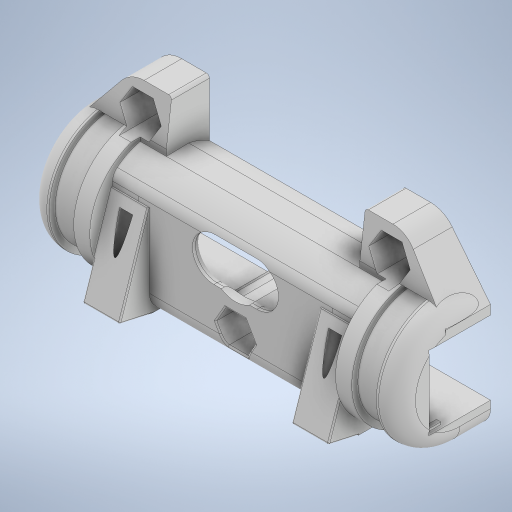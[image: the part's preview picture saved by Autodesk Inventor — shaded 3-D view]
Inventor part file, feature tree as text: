
AUTODESK INVENTOR PART (.ipt)
format: ipt  version: 2023 (Build 270158000, 158)  size: 2,027,008 bytes
history: native  units: mm
features: extrude x61, projected_geometry x60, sketch x41, fillet x6, mirror x3, plane x2
ambient origin geometry x8: Origin, YZ Plane, XZ Plane, XY Plane, X Axis, Y Axis, Z Axis, Center Point
bodies: Solid1 (feature_tree)
feature tree (173):
  extrude  "Extrusion1"  Depth=0.6mm
  extrude  "Extrusion2"  Depth=5.1mm
  extrude  "Extrusion3"  Depth=11.5mm TaperAngle=0.0deg
  extrude  "Extrusion4"  Depth=1.0mm
  extrude  "Extrusion5"  Depth=2.5mm TaperAngle=0.0deg
  mirror  "Mirror1"
  extrude  "Extrusion6"  Depth=30.0mm TaperAngle=0.0deg
  extrude  "Extrusion7"  Depth=3.5mm
  extrude  "Extrusion8"  Depth=37.5mm
  extrude  "Extrusion9"  Depth=1.5mm
  extrude  "Extrusion10"  Depth=4.0mm TaperAngle=0.0deg
  fillet  "Fillet1"  Radius=2.75mm
  extrude  "Extrusion11"  Depth=2.7mm
  sketch  "Sketch13"  dims[d37=2.0mm d38=0.0mm d39=3.0mm d40=0.0mm]
  extrude  "Extrusion12"  Depth=3.0mm TaperAngle=0.0deg
  extrude  "Extrusion13"  Depth=0.5mm
  extrude  "Extrusion14"  Depth=5.0mm
  extrude  "Extrusion15"  Depth=2.0mm TaperAngle=0.0deg
  extrude  "Extrusion16"  Depth=5.0mm
  extrude  "Extrusion17"  Depth=1.0mm
  extrude  "Extrusion18"  Depth=14.25mm TaperAngle=0.0deg
  sketch  "Sketch14"  dims[d41=7.0mm d42=0.0mm d43=0.5mm]
  extrude  "Extrusion19"  Depth=14.25mm TaperAngle=0.0deg
  extrude  "Extrusion20"  Depth=14.25mm TaperAngle=0.0deg
  plane  "Work Plane1"
  extrude  "Extrusion21"  Depth=2.5mm TaperAngle=0.0deg
  extrude  "Extrusion22"  Depth=4.0mm TaperAngle=0.0deg
  sketch  "Sketch17"  dims[d49=30.4mm d52=5.0mm]
  extrude  "Extrusion23"  Depth=14.25mm TaperAngle=0.0deg
  extrude  "Extrusion24"  Depth=14.25mm TaperAngle=0.0deg
  extrude  "Extrusion25"  Depth=14.25mm TaperAngle=0.0deg
  fillet  "Fillet3"  Radius=0.5mm
  extrude  "Extrusion26"  Depth=10.0mm TaperAngle=0.0deg
  extrude  "Extrusion27"  TaperAngle=0.0deg  [1 undecoded]
  extrude  "Extrusion28"  TaperAngle=0.0deg  [1 undecoded]
  extrude  "Extrusion29"  Depth=3.0mm TaperAngle=0.0deg
  extrude  "Extrusion30"  TaperAngle=0.0deg  [1 undecoded]
  sketch  "Sketch24"  dims[d75=2.5mm d76=0.0mm d77=14.25mm d78=0.0mm]
  extrude  "Extrusion31"  Depth=10.0mm TaperAngle=0.0deg
  extrude  "Extrusion32"  Depth=10.0mm TaperAngle=0.0deg
  sketch  "Sketch25"  dims[d79=14.25mm d80=0.0mm d82=14.25mm d83=0.0mm]
  extrude  "Extrusion33"  Depth=7.5mm TaperAngle=0.0deg
  extrude  "Extrusion34"  TaperAngle=0.0deg  [1 undecoded]
  extrude  "Extrusion35"  Depth=22.0mm TaperAngle=0.0deg
  extrude  "Extrusion36"  Depth=10.0mm TaperAngle=0.0deg
  sketch  "Sketch26"  dims[d84=2.0mm d85=14.25mm d86=0.0mm d87=0.5mm]
  extrude  "Extrusion37"  Depth=10.0mm TaperAngle=0.0deg
  extrude  "Extrusion38"  Depth=4.0mm TaperAngle=0.0deg
  extrude  "Extrusion39"  Depth=29.237756mm
  extrude  "Extrusion40"  Depth=6.0mm TaperAngle=0.0deg
  mirror  "Mirror2"
  extrude  "Extrusion41"  Depth=10.0mm
  fillet  "Fillet4"  Radius=13.0mm
  extrude  "Extrusion42"  Depth=10.0mm
  extrude  "Extrusion43"  Depth=10.0mm
  extrude  "Extrusion44"  TaperAngle=0.0deg  [1 undecoded]
  sketch  "Sketch34"  dims[d113=10.0mm d114=0.0mm d115=1.0mm d116=0.0mm]
  extrude  "Extrusion47"  Depth=10.0mm
  extrude  "Extrusion48"  Depth=10.0mm
  extrude  "Extrusion49"  Depth=10.0mm TaperAngle=0.0deg
  sketch  "Sketch35"  dims[d117=7.5mm d118=0.0mm d119=7.5mm d120=0.0mm]
  extrude  "Extrusion50"  TaperAngle=0.0deg  [1 undecoded]
  extrude  "Extrusion51"  Depth=10.0mm TaperAngle=0.0deg
  extrude  "Extrusion52"  Depth=10.0mm TaperAngle=0.0deg
  extrude  "Extrusion53"  TaperAngle=0.0deg  [1 undecoded]
  sketch  "Sketch38"  dims[d133=10.0mm d134=0.0mm d135=7.375mm d136=0.0mm]
  extrude  "Extrusion54"  Depth=10.0mm
  extrude  "Extrusion55"  Depth=10.0mm
  extrude  "Extrusion56"  Depth=10.0mm
  extrude  "Extrusion57"  Depth=10.0mm TaperAngle=0.0deg
  sketch  "Sketch41"  dims[d145=15.75mm d146=0.0mm d147=29.237756mm]
  extrude  "Extrusion58"  [1 undecoded]
  extrude  "Extrusion59"  [1 undecoded]
  extrude  "Extrusion60"  [1 undecoded]
  sketch  "Sketch42"  dims[d148=5.0mm d149=6.0mm d150=0.0mm]
  extrude  "Extrusion61"  [1 undecoded]
  extrude  "Extrusion62"  [1 undecoded]
  fillet  "Fillet5"  [1 undecoded]
  fillet  "Fillet6"  [1 undecoded]
  fillet  "Fillet7"  [1 undecoded]
  extrude  "Extrusion63"  [1 undecoded]
  mirror  "Mirror3"
  sketch  "Sketch1"  dims[d0=11.5mm d1=0.0mm d2=0.6mm]
  sketch  "Sketch2"  dims[d3=0.7mm d4=5.1mm]
  projected_geometry  "Projected Loop1"
  projected_geometry  "Projected Loop2"
  sketch  "Sketch3"  dims[d5=2.0mm d6=11.5mm d7=0.0mm]
  sketch  "Sketch4"  dims[d8=1.0mm d9=1.0mm]
  sketch  "Sketch6"  dims[d10=1.0mm d11=2.5mm d12=0.0mm]
  projected_geometry  "Projected Loop3"
  sketch  "Sketch7"  dims[d13=0.1mm d14=0.0mm d21=30.0mm d22=0.0mm]
  projected_geometry  "Projected Loop4"
  projected_geometry  "Projected Loop5"
  projected_geometry  "Projected Loop6"
  sketch  "Sketch8"  dims[d23=44.0mm d24=3.5mm]
  projected_geometry  "Projected Loop7"
  projected_geometry  "Projected Loop8"
  sketch  "Sketch9"  dims[d25=3.0mm d27=37.5mm]
  projected_geometry  "Projected Loop9"
  sketch  "Sketch10"  dims[d28=1.5mm d29=1.5mm]
  projected_geometry  "Projected Loop10"
  sketch  "Sketch11"  dims[d30=3.0mm d31=4.0mm d32=0.0mm d33=2.75mm d34=0.0mm]
  projected_geometry  "Projected Loop11"
  sketch  "Sketch12"  dims[d35=2.7mm d36=2.7mm]
  projected_geometry  "Projected Loop12"
  projected_geometry  "Projected Loop13"
  projected_geometry  "Projected Loop14"
  projected_geometry  "Projected Loop15"
  projected_geometry  "Projected Loop16"
  projected_geometry  "Projected Loop17"
  projected_geometry  "Projected Loop18"
  sketch  "Sketch15"  dims[d44=31.0mm d45=5.0mm]
  sketch  "Sketch16"  dims[d46=3.0mm d47=2.0mm d48=0.0mm]
  projected_geometry  "Projected Loop19"
  projected_geometry  "Projected Loop20"
  projected_geometry  "Projected Loop21"
  projected_geometry  "Projected Loop22"
  sketch  "Sketch18"  dims[d53=2.0mm d54=1.0mm]
  projected_geometry  "Projected Loop23"
  sketch  "Sketch19"  dims[d55=15.0mm d56=0.0mm d57=14.25mm d58=0.0mm]
  projected_geometry  "Projected Loop24"
  projected_geometry  "Projected Loop25"
  sketch  "Sketch20"  dims[d59=14.25mm d60=0.0mm d61=14.25mm d62=0.0mm]
  projected_geometry  "Projected Loop26"
  sketch  "Sketch21"  dims[d63=14.25mm d64=0.0mm d65=14.25mm d66=0.0mm]
  projected_geometry  "Projected Loop27"
  projected_geometry  "Projected Loop28"
  sketch  "Sketch22"  dims[d67=2.5mm d68=0.0mm d69=2.5mm d70=0.0mm]
  projected_geometry  "Projected Loop29"
  sketch  "Sketch23"  dims[d71=2.5mm d72=0.0mm d73=4.0mm d74=0.0mm]
  projected_geometry  "Projected Loop30"
  projected_geometry  "Projected Loop31"
  projected_geometry  "Projected Loop32"
  projected_geometry  "Projected Loop33"
  projected_geometry  "Projected Loop34"
  projected_geometry  "Projected Loop35"
  projected_geometry  "Projected Loop36"
  sketch  "Sketch27"  dims[d88=0.0mm d89=0.0mm d90=10.0mm d91=0.0mm]
  projected_geometry  "Projected Loop37"
  sketch  "Sketch28"  dims[d92=0.0mm d93=0.0mm d94=0.0mm d95=0.0mm]
  projected_geometry  "Projected Loop38"
  plane  "Work Plane2"
  sketch  "Sketch29"  dims[d96=1.0mm d97=0.0mm d98=0.0mm d99=0.0mm]
  projected_geometry  "Projected Loop39"
  sketch  "Sketch30"  dims[d100=8.0mm d101=0.0mm d102=3.0mm d103=0.0mm]
  projected_geometry  "Projected Loop40"
  projected_geometry  "Projected Loop41"
  sketch  "Sketch31"  dims[d104=1.75mm d105=2.25mm d106=0.0mm d107=0.0mm d108=0.0mm d109=0.0mm]
  projected_geometry  "Projected Loop42"
  projected_geometry  "Projected Loop43"
  sketch  "Sketch32"  dims[d110=3.5mm d111=10.0mm d112=0.0mm]
  projected_geometry  "Projected Loop45"
  projected_geometry  "Projected Loop46"
  projected_geometry  "Projected Loop47"
  projected_geometry  "Projected Loop48"
  projected_geometry  "Projected Loop49"
  sketch  "Sketch36"  dims[d121=0.2mm d122=0.0mm d123=0.0mm]
  projected_geometry  "Projected Loop50"
  sketch  "Sketch37"  dims[d124=6.0mm d125=0.0mm d126=22.0mm d127=0.0mm]
  projected_geometry  "Projected Loop51"
  projected_geometry  "Projected Loop52"
  projected_geometry  "Projected Loop53"
  sketch  "Sketch39"  dims[d137=3.375mm d138=0.0mm d139=10.0mm d140=0.0mm]
  projected_geometry  "Projected Loop54"
  sketch  "Sketch40"  dims[d141=5.0mm d142=0.0mm d143=4.0mm d144=0.0mm]
  projected_geometry  "Projected Loop55"
  projected_geometry  "Projected Loop56"
  projected_geometry  "Projected Loop57"
  projected_geometry  "Projected Loop58"
  projected_geometry  "Projected Loop59"
  projected_geometry  "Projected Loop60"
  sketch  "Sketch43"  dims[d151=8.0mm d152=0.0mm d153=2.5mm d154=13.0mm d155=0.0mm d156=6.0mm d157=7.0mm d158=0.0mm d159=0.0mm d160=3.0mm d161=2.8mm d162=11.5mm d163=0.0mm d164=0.0mm d165=0.0mm d166=7.8mm d167=0.0mm d168=10.0mm d169=0.0mm d170=0.0mm d171=0.0mm d172=3.0mm d173=0.2mm d174=1.0mm d175=0.25mm d176=0.0mm]
  projected_geometry  "Projected Loop61"
note: 16 required parameter values undecoded (feature->parameter linkage not recoverable at this tier; creation-order binding heuristic only, values carry confidence <= 0.55)
